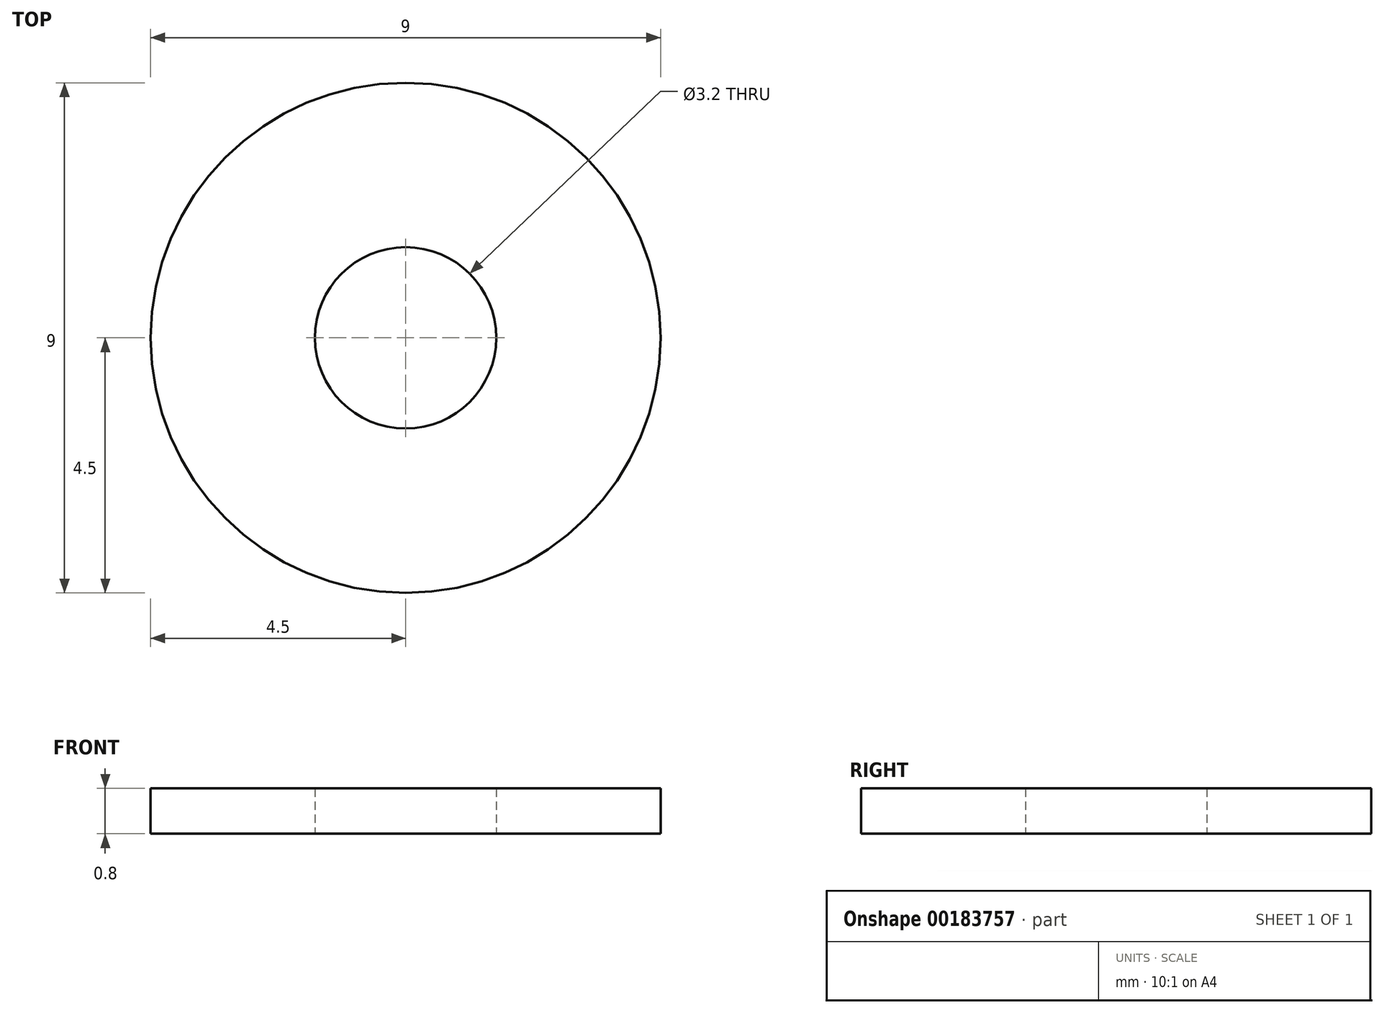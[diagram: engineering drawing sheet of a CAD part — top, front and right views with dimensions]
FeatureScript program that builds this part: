
annotation { "Feature Type Name" : "Feature", "Feature Type Description" : "" }
export const myFeature = defineFeature(function(context is Context, id is Id, definition is map)
    precondition{}
    {
        {
            var Q0;
            Q0=qCreatedBy(makeId("Top.planeOp"),FACE);
            var sketch = newSketch(context, id + "F0", { "sketchPlane" : qUnion([Q0])});
            skCircle(sketch, "E0", {"center": v(0, 0) * mm, "radius": 4.5 * mm});
            skCircle(sketch, "E1", {"center": v(0, 0) * mm, "radius": 1.6 * mm});
            skSolve(sketch);
        }
        {
            var Q0;
            Q0=makeQuery(id+"F0.imprint","IMPRINT",FACE,{"disambiguationData":[TD([[makeQuery(id+"F0.imprint","IMPRINT",EDGE,{"derivedFrom":sQuery(id+"F0.wireOp",EDGE,"E0")}),1.0]])]});
            var sketch = newSketch(context, id + "F1", { "sketchPlane" : qUnion([Q0])});
            skSolve(sketch);
        }
        {
            var Q0;
            Q0 = qSketchRegion(id + "F1", true);
            var Q1;
            Q1=makeQuery(id+"F0.imprint","IMPRINT",FACE,{"disambiguationData":[TD([[makeQuery(id+"F0.imprint","IMPRINT",EDGE,{"derivedFrom":sQuery(id+"F0.wireOp",EDGE,"E0")}),1.0]])]});
            extrude(context, id + "F2", {"entities" : qUnion([Q0, Q1]), "depth" : .8 * mm});
        }
    });
